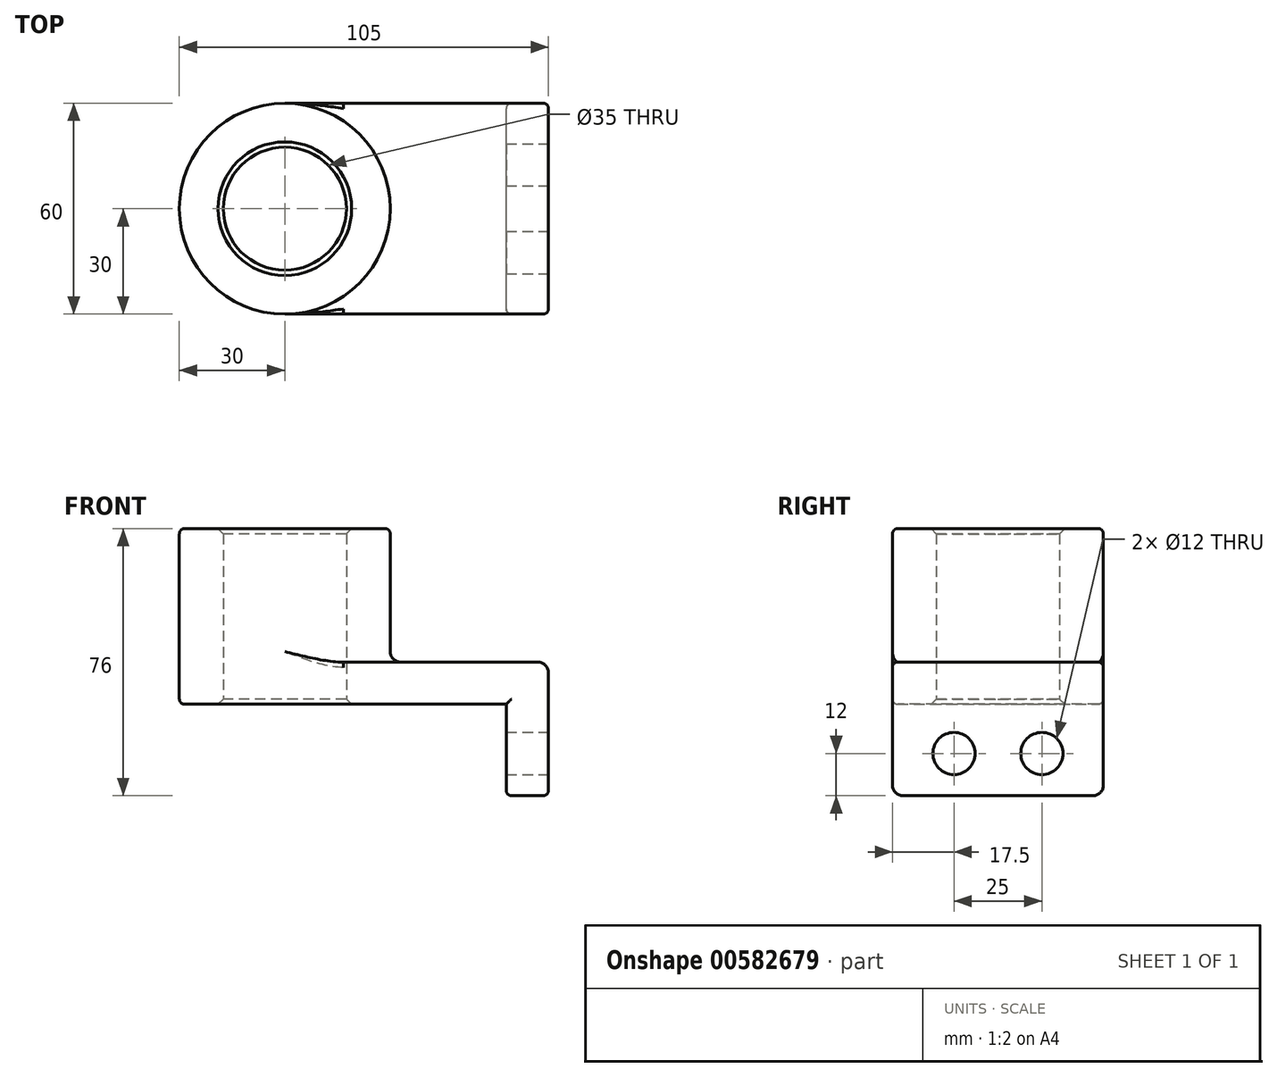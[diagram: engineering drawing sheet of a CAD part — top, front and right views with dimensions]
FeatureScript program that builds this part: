
annotation { "Feature Type Name" : "Feature", "Feature Type Description" : "" }
export const myFeature = defineFeature(function(context is Context, id is Id, definition is map)
    precondition{}
    {
        {
            var Q0;
            Q0=qCreatedBy(makeId("Top.planeOp"),FACE);
            var sketch = newSketch(context, id + "F0", { "sketchPlane" : qUnion([Q0])});
            skLineSegment(sketch, "E0.bottom", {"start": v(-37.5, -30) * mm, "end": v(37.5, -30) * mm});
            skLineSegment(sketch, "E0.top", {"start": v(-37.5, 30) * mm, "end": v(37.5, 30) * mm});
            skLineSegment(sketch, "E0.left", {"start": v(-37.5, -30) * mm, "end": v(-37.5, 30) * mm});
            skLineSegment(sketch, "E0.right", {"start": v(37.5, -30) * mm, "end": v(37.5, 30) * mm});
            skPoint(sketch, "E0.middle", {"position": v(0, 0) * mm});
            skCircle(sketch, "E1", {"center": v(-37.5, 0) * mm, "radius": 30 * mm});
            skCircle(sketch, "E2", {"center": v(-37.5, 0) * mm, "radius": 17.5 * mm});
            skSolve(sketch);
        }
        {
            var Q0;
            Q0 = qSketchRegion(id + "F0", true);
            extrude(context, id + "F1", {"entities" : qUnion([Q0]), "depth" : 12 * mm, "offsetDistance" : 25 * mm});
        }
        {
            var Q0;
            {var subQ1=sQuery(id+"F0.wireOp",EDGE,"E0.left");var subQ3=sQuery(id+"F0.wireOp",EDGE,"E2");var subQ4=makeQuery(id+"F0.imprint","INTERSECT",VERTEX,{"disambiguationData":[OD(0.0)],"derivedFrom":[subQ1,subQ3]});Q0=makeQuery(id+"F0.imprint","IMPRINT",FACE,{"disambiguationData":[TD([[makeQuery(id+"F0.imprint","IMPRINT",EDGE,{"disambiguationData":[TD([[subQ4,1.0]])],"derivedFrom":subQ3}),-1.0]])]});}
            var Q1;
            {var subQ1=sQuery(id+"F0.wireOp",EDGE,"E0.left");var subQ3=sQuery(id+"F0.wireOp",EDGE,"E2");var subQ4=makeQuery(id+"F0.imprint","INTERSECT",VERTEX,{"disambiguationData":[OD(0.0)],"derivedFrom":[subQ1,subQ3]});Q1=makeQuery(id+"F0.imprint","IMPRINT",FACE,{"disambiguationData":[TD([[makeQuery(id+"F0.imprint","IMPRINT",EDGE,{"disambiguationData":[TD([[subQ4,-1.0]])],"derivedFrom":subQ3}),-1.0]])]});}
            extrude(context, id + "F2", {"entities" : qUnion([Q0, Q1]), "operationType" : NewBodyOperationType.ADD, "depth" : 50 * mm, "offsetDistance" : 25 * mm});
        }
        {
            var Q0;
            Q0=makeQuery(id+"F1.opExtrude","SWEPT_FACE",FACE,{"disambiguationData":[OSD([sQuery(id+"F0.wireOp",EDGE,"E0.right")])]});
            var sketch = newSketch(context, id + "F3", { "sketchPlane" : qUnion([Q0])});
            skLineSegment(sketch, "E3.bottom", {"start": v(-30, 12) * mm, "end": v(30, 12) * mm});
            skLineSegment(sketch, "E3.top", {"start": v(-30, -26) * mm, "end": v(30, -26) * mm});
            skLineSegment(sketch, "E3.left", {"start": v(-30, 12) * mm, "end": v(-30, -26) * mm});
            skLineSegment(sketch, "E3.right", {"start": v(30, 12) * mm, "end": v(30, -26) * mm});
            skCircle(sketch, "E4", {"center": v(-12.5, -14) * mm, "radius": 6 * mm});
            skLineSegment(sketch, "E5", {"start": v(0, 0) * mm, "end": v(0, -26) * mm, "construction": true});
            skCircle(sketch, "E6.MirrorC", {"center": v(12.5, -14) * mm, "radius": 6 * mm});
            skSolve(sketch);
        }
        {
            var Q0;
            Q0 = qSketchRegion(id + "F3", true);
            extrude(context, id + "F4", {"entities" : qUnion([Q0]), "operationType" : NewBodyOperationType.ADD, "depth" : -12 * mm, "offsetDistance" : 25 * mm});
        }
        {
            var Q0;
            {var subQ0=sQuery(id+"F0.wireOp",EDGE,"E1");Q0=makeQuery(id+"F2.boolean.opBoolean","INTERSECT",EDGE,{"derivedFrom":[makeQuery(id+"F1.opExtrude","CAP_FACE",FACE,{"disambiguationData":[OSD([sQuery(id+"F0.wireOp",EDGE,"E0.bottom"),sQuery(id+"F0.wireOp",EDGE,"E0.top"),sQuery(id+"F0.wireOp",EDGE,"E0.right"),subQ0,sQuery(id+"F0.wireOp",EDGE,"E2")])],"isStart":false}),makeQuery(id+"F2.opExtrude","SWEPT_FACE",FACE,{"disambiguationData":[OSD([subQ0])]})]});}
            var Q1;
            Q1=makeQuery(id+"F4.opExtrude","SWEPT_EDGE",EDGE,{"disambiguationData":[OSD([sQuery(id+"F3.wireOp",EDGE,"E3.top"),sQuery(id+"F3.wireOp",EDGE,"E3.left")])]});
            var Q2;
            Q2=makeQuery(id+"F4.opExtrude","SWEPT_EDGE",EDGE,{"disambiguationData":[OSD([sQuery(id+"F3.wireOp",EDGE,"E3.top"),sQuery(id+"F3.wireOp",EDGE,"E3.right")])]});
            var Q3;
            Q3=makeQuery(id+"F1.opExtrude","CAP_EDGE",EDGE,{"disambiguationData":[OSD([sQuery(id+"F0.wireOp",EDGE,"E0.right")])],"isStart":false});
            fillet(context, id + "F5", {"entities" : qUnion([Q0, Q1, Q2, Q3]), "radius" : 3 * mm, "tangentPropagation" : true, "allowEdgeOverflow" : false});
        }
        {
            var Q0;
            Q0=makeQuery(id+"F1.opExtrude","CAP_EDGE",EDGE,{"disambiguationData":[OSD([sQuery(id+"F0.wireOp",EDGE,"E0.bottom")])],"isStart":false});
            var Q1;
            Q1=makeQuery(id+"F1.opExtrude","CAP_EDGE",EDGE,{"disambiguationData":[OSD([sQuery(id+"F0.wireOp",EDGE,"E0.bottom")])],"isStart":true});
            var Q2;
            Q2=makeQuery(id+"F4.opExtrude","CAP_EDGE",EDGE,{"disambiguationData":[OSD([sQuery(id+"F3.wireOp",EDGE,"E3.left")])],"isStart":false});
            fillet(context, id + "F6", {"entities" : qUnion([Q0, Q1, Q2]), "radius" : 1.5 * mm, "tangentPropagation" : true, "allowEdgeOverflow" : false});
        }
        {
            var Q0;
            {var subQ0=sQuery(id+"F0.wireOp",EDGE,"E2");Q0=makeQuery(id+"F2.boolean.opBoolean","MERGE",FACE,{"derivedFrom":[makeQuery(id+"F1.opExtrude","SWEPT_FACE",FACE,{"disambiguationData":[OSD([subQ0])]}),makeQuery(id+"F2.opExtrude","SWEPT_FACE",FACE,{"disambiguationData":[OSD([subQ0])]})]});}
            chamfer(context, id + "F7", {"entities" : qUnion([Q0]), "width" : 1.5 * mm, "tangentPropagation" : true});
        }
        {
            var Q0;
            Q0=makeQuery(id+"F2.opExtrude","CAP_EDGE",EDGE,{"disambiguationData":[OSD([sQuery(id+"F0.wireOp",EDGE,"E1")])],"isStart":false});
            fillet(context, id + "F8", {"entities" : qUnion([Q0]), "radius" : 1.5 * mm, "tangentPropagation" : true, "allowEdgeOverflow" : false});
        }
    });
